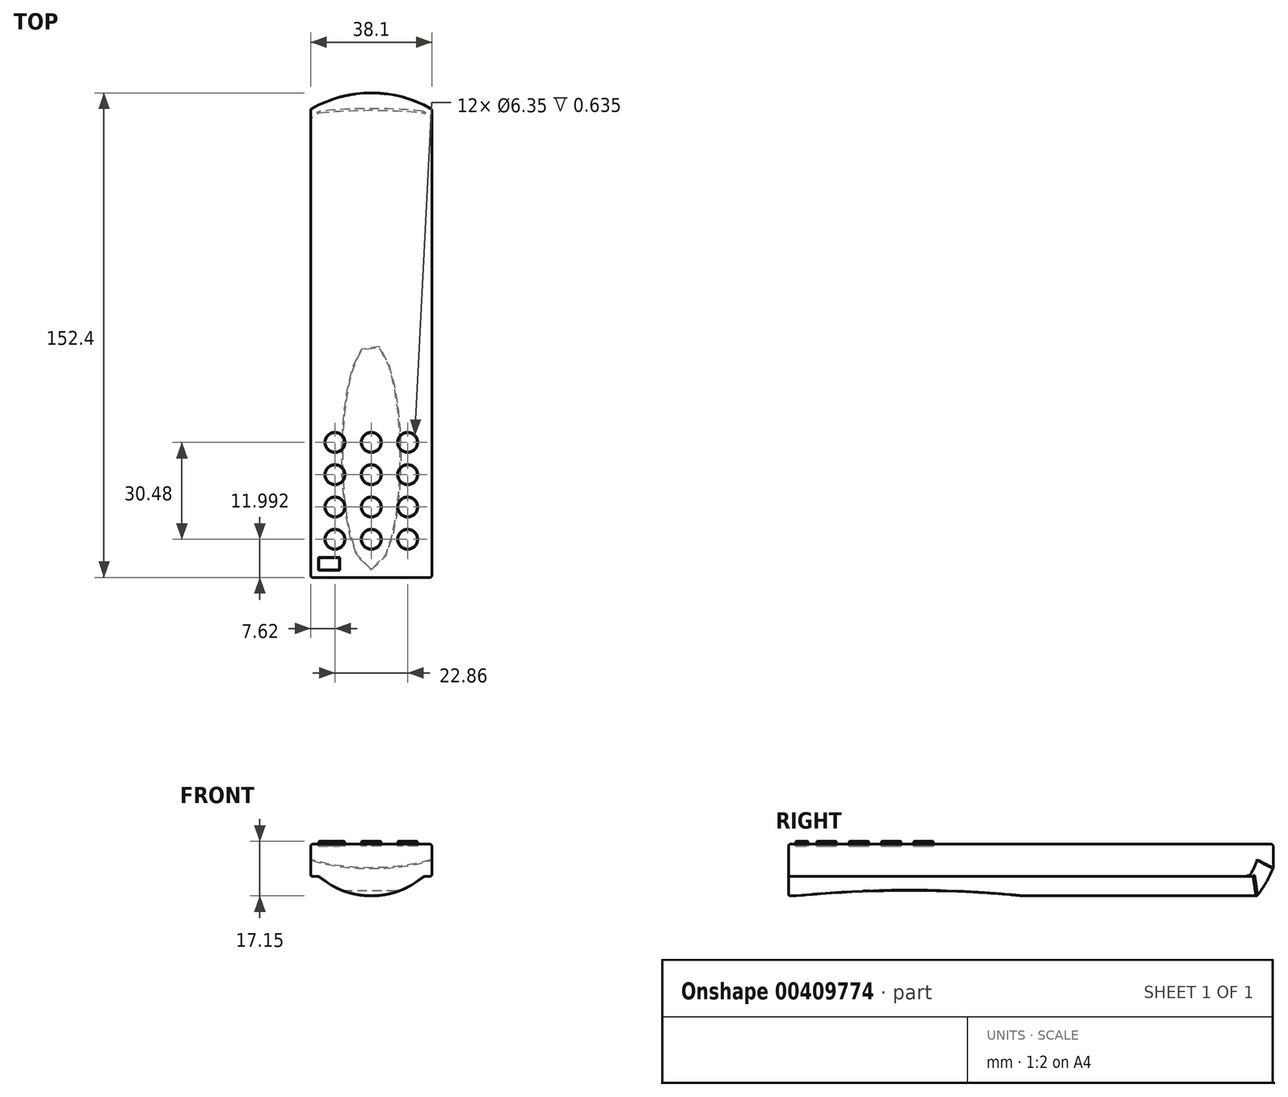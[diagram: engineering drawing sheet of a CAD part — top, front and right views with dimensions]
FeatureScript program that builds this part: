
annotation { "Feature Type Name" : "Feature", "Feature Type Description" : "" }
export const myFeature = defineFeature(function(context is Context, id is Id, definition is map)
    precondition{}
    {
        {
            var Q0;
            Q0=qCreatedBy(makeId("Front.planeOp"),FACE);
            var sketch = newSketch(context, id + "F0", { "sketchPlane" : qUnion([Q0])});
            skLineSegment(sketch, "E0.bottom", {"start": v(19.05, 5.08) * mm, "end": v(-19.05, 5.08) * mm});
            skLineSegment(sketch, "E0.top", {"start": v(19.05, -5.08) * mm, "end": v(-19.05, -5.08) * mm});
            skLineSegment(sketch, "E0.left", {"start": v(19.05, 5.08) * mm, "end": v(19.05, -5.08) * mm});
            skLineSegment(sketch, "E0.right", {"start": v(-19.05, 5.08) * mm, "end": v(-19.05, -5.08) * mm});
            skPoint(sketch, "E0.middle", {"position": v(0, 0) * mm});
            skArc(sketch, "E1", {"start": v(-16.51, -5.08) * mm, "mid": v(0, -11.18) * mm, "end": v(16.5, -5.08) * mm});
            skSolve(sketch);
        }
        {
            var Q0;
            Q0 = qSketchRegion(id + "F0", true);
            extrude(context, id + "F1", {"entities" : qUnion([Q0]), "depth" : 152.4 * mm, "symmetric" : true});
        }
        {
            var Q0;
            Q0=makeQuery(id+"F1.opExtrude","SWEPT_FACE",FACE,{"disambiguationData":[OSD([sQuery(id+"F0.wireOp",EDGE,"E0.bottom")])]});
            var sketch = newSketch(context, id + "F2", { "sketchPlane" : qUnion([Q0])});
            skArc(sketch, "E2", {"start": v(19.05, 71.1) * mm, "mid": v(0, 76.2) * mm, "end": v(-19.05, 71.1) * mm});
            skLineSegment(sketch, "E3", {"start": v(0, -0.47) * mm, "end": v(0, 76.2) * mm, "construction": true});
            skSolve(sketch);
        }
        {
            var Q0;
            {var subQ0=sQuery(id+"F2.wireOp",EDGE,"E2");var subQ1=sQuery(id+"F0.wireOp",EDGE,"E0.bottom");var subQ4=makeQuery(id+"F1.opExtrude","CAP_EDGE",EDGE,{"disambiguationData":[OSD([subQ1])],"isStart":true});var subQ5=makeQuery(id+"F2.imprint","INTERSECT",VERTEX,{"derivedFrom":[subQ4,subQ0]});Q0=makeQuery(id+"F2.imprint","IMPRINT",FACE,{"disambiguationData":[TD([[makeQuery(id+"F2.imprint","IMPRINT",EDGE,{"disambiguationData":[TD([[subQ5,1.0]])],"derivedFrom":subQ0}),-1.0]])]});}
            var Q1;
            {var subQ0=sQuery(id+"F2.wireOp",EDGE,"E2");var subQ1=sQuery(id+"F0.wireOp",EDGE,"E0.bottom");var subQ4=makeQuery(id+"F1.opExtrude","CAP_EDGE",EDGE,{"disambiguationData":[OSD([subQ1])],"isStart":true});var subQ5=makeQuery(id+"F2.imprint","INTERSECT",VERTEX,{"derivedFrom":[subQ4,subQ0]});Q1=makeQuery(id+"F2.imprint","IMPRINT",FACE,{"disambiguationData":[TD([[makeQuery(id+"F2.imprint","IMPRINT",EDGE,{"disambiguationData":[TD([[subQ5,-1.0]])],"derivedFrom":subQ0}),-1.0]])]});}
            extrude(context, id + "F3", {"entities" : qUnion([Q0, Q1]), "operationType" : NewBodyOperationType.REMOVE, "endBound" : BoundingType.THROUGH_ALL, "oppositeDirection" : true, "depth" : 25.4 * mm});
        }
        {
            var Q0;
            Q0=qCreatedBy(makeId("Right.planeOp"),FACE);
            var sketch = newSketch(context, id + "F4", { "sketchPlane" : qUnion([Q0])});
            skArc(sketch, "E4", {"start": v(64.41, -17.52) * mm, "mid": v(76.76, -0.97) * mm, "end": v(77.47, 19.67) * mm});
            skCircle(sketch, "E5", {"center": v(44.14, 10.48) * mm, "radius": 34.57 * mm});
            skLineSegment(sketch, "E6", {"start": v(44.14, 45.05) * mm, "end": v(44.14, -24.1) * mm});
            skLineSegment(sketch, "E7.bottom", {"start": v(44.14, 45.05) * mm, "end": v(78.38, 45.05) * mm});
            skLineSegment(sketch, "E7.top", {"start": v(44.14, -24.1) * mm, "end": v(78.38, -24.1) * mm});
            skLineSegment(sketch, "E7.right", {"start": v(78.38, 45.05) * mm, "end": v(78.38, -24.1) * mm});
            skSolve(sketch);
        }
        {
            var Q0;
            {var subQ0=sQuery(id+"F4.wireOp",EDGE,"E7.top");Q0=makeQuery(id+"F4.imprint","IMPRINT",FACE,{"disambiguationData":[TD([[makeQuery(id+"F4.imprint","IMPRINT",EDGE,{"derivedFrom":subQ0}),1.0]])]});}
            var Q1;
            Q1=sQuery(id+"F4.wireOp",EDGE,"E6");
            revolve(context, id + "F5", {"operationType" : NewBodyOperationType.REMOVE, "entities" : qUnion([Q0]), "axis" : qUnion([Q1]), "revolveType" : RevolveType.SYMMETRIC, "oppositeDirection" : true, "angle" : 90 * degree});
        }
        {
            var Q0;
            Q0=makeQuery(id+"F5.boolean.opBoolean","COPY",FACE,{"derivedFrom":makeQuery(id+"F5.opRevolve","SWEPT_FACE",FACE,{"disambiguationData":[OSD([sQuery(id+"F4.wireOp",EDGE,"E5")])]})});
            var Q1;
            {var subQ0=sQuery(id+"F2.wireOp",EDGE,"E2");var subQ1=sQuery(id+"F0.wireOp",EDGE,"E0.bottom");var subQ2=makeQuery(id+"F2.imprint","INTERSECT",VERTEX,{"derivedFrom":[makeQuery(id+"F1.opExtrude","CAP_EDGE",EDGE,{"disambiguationData":[OSD([subQ1])],"isStart":true}),subQ0]});Q1=makeQuery(id+"F3.boolean.opBoolean","MERGE",FACE,{"derivedFrom":[],"fromTools":[makeQuery(id+"F3.opExtrude","SWEPT_FACE",FACE,{"disambiguationData":[OSD([subQ0]),TDD([makeQuery(id+"F2.imprint","IMPRINT",EDGE,{"disambiguationData":[TD([[subQ2,1.0]])],"derivedFrom":subQ0})])]}),makeQuery(id+"F3.opExtrude","SWEPT_FACE",FACE,{"disambiguationData":[OSD([subQ0]),TDD([makeQuery(id+"F2.imprint","IMPRINT",EDGE,{"disambiguationData":[TD([[subQ2,-1.0]])],"derivedFrom":subQ0})])]})]});}
            var Q2;
            Q2=makeQuery(id+"F1.opExtrude","SWEPT_FACE",FACE,{"disambiguationData":[OSD([sQuery(id+"F0.wireOp",EDGE,"E0.bottom")])]});
            var Q3;
            Q3=makeQuery(id+"F1.opExtrude","SWEPT_FACE",FACE,{"disambiguationData":[OSD([sQuery(id+"F0.wireOp",EDGE,"E0.right")])]});
            var Q4;
            Q4=makeQuery(id+"F1.opExtrude","SWEPT_FACE",FACE,{"disambiguationData":[OSD([sQuery(id+"F0.wireOp",EDGE,"E1")])]});
            var Q5;
            {var subQ0=sQuery(id+"F0.wireOp",EDGE,"E0.top");Q5=makeQuery(id+"F1.opExtrude","SWEPT_FACE",FACE,{"disambiguationData":[OSD([subQ0]),TDD([makeQuery(id+"F0.imprint","IMPRINT",EDGE,{"disambiguationData":[TD([[makeQuery(id+"F0.imprint","INTERSECT",VERTEX,{"derivedFrom":[subQ0,sQuery(id+"F0.wireOp",EDGE,"E0.right")]}),1.0]])],"derivedFrom":subQ0})])]});}
            var Q6;
            {var subQ0=sQuery(id+"F0.wireOp",EDGE,"E0.top");Q6=makeQuery(id+"F1.opExtrude","SWEPT_FACE",FACE,{"disambiguationData":[OSD([subQ0]),TDD([makeQuery(id+"F0.imprint","IMPRINT",EDGE,{"disambiguationData":[TD([[makeQuery(id+"F0.imprint","INTERSECT",VERTEX,{"derivedFrom":[subQ0,sQuery(id+"F0.wireOp",EDGE,"E0.left")]}),-1.0]])],"derivedFrom":subQ0})])]});}
            var Q7;
            Q7=makeQuery(id+"F1.opExtrude","SWEPT_FACE",FACE,{"disambiguationData":[OSD([sQuery(id+"F0.wireOp",EDGE,"E0.left")])]});
            var Q8;
            Q8=makeQuery(id+"F1.opExtrude","CAP_FACE",FACE,{"disambiguationData":[OSD([sQuery(id+"F0.wireOp",EDGE,"E0.bottom"),sQuery(id+"F0.wireOp",EDGE,"E0.top"),sQuery(id+"F0.wireOp",EDGE,"E0.left"),sQuery(id+"F0.wireOp",EDGE,"E0.right"),sQuery(id+"F0.wireOp",EDGE,"E1")])],"isStart":false});
            fillet(context, id + "F6", {"entities" : qUnion([Q0, Q1, Q2, Q3, Q4, Q5, Q6, Q7, Q8]), "radius" : 0.64 * mm, "tangentPropagation" : true, "allowEdgeOverflow" : false});
        }
        {
            var Q0;
            Q0=makeQuery(id+"F1.opExtrude","SWEPT_FACE",FACE,{"disambiguationData":[OSD([sQuery(id+"F0.wireOp",EDGE,"E0.bottom")])]});
            var sketch = newSketch(context, id + "F7", { "sketchPlane" : qUnion([Q0])});
            skLineSegment(sketch, "E8.bottom", {"start": v(-16.6, -74) * mm, "end": v(-9.92, -74) * mm});
            skLineSegment(sketch, "E8.top", {"start": v(-16.6, -69.92) * mm, "end": v(-9.92, -69.92) * mm});
            skLineSegment(sketch, "E8.left", {"start": v(-16.6, -74) * mm, "end": v(-16.6, -69.92) * mm});
            skLineSegment(sketch, "E8.right", {"start": v(-9.92, -74) * mm, "end": v(-9.92, -69.92) * mm});
            skCircle(sketch, "E9", {"center": v(11.43, -64.2) * mm, "radius": 3.18 * mm});
            skCircle(sketch, "E10.0.1.0", {"center": v(11.43, -54.05) * mm, "radius": 3.18 * mm});
            skCircle(sketch, "E10.0.2.0", {"center": v(11.43, -43.89) * mm, "radius": 3.18 * mm});
            skCircle(sketch, "E10.0.3.0", {"center": v(11.43, -33.73) * mm, "radius": 3.18 * mm});
            skCircle(sketch, "E10.1.0.0", {"center": v(0, -64.2) * mm, "radius": 3.18 * mm});
            skCircle(sketch, "E10.1.1.0", {"center": v(0, -54.05) * mm, "radius": 3.18 * mm});
            skCircle(sketch, "E10.1.2.0", {"center": v(0, -43.89) * mm, "radius": 3.18 * mm});
            skCircle(sketch, "E10.1.3.0", {"center": v(0, -33.73) * mm, "radius": 3.18 * mm});
            skCircle(sketch, "E10.2.0.0", {"center": v(-11.43, -64.2) * mm, "radius": 3.18 * mm});
            skCircle(sketch, "E10.2.1.0", {"center": v(-11.43, -54.05) * mm, "radius": 3.18 * mm});
            skCircle(sketch, "E10.2.2.0", {"center": v(-11.43, -43.89) * mm, "radius": 3.18 * mm});
            skCircle(sketch, "E10.2.3.0", {"center": v(-11.43, -33.73) * mm, "radius": 3.18 * mm});
            skLineSegment(sketch, "E10.direction1", {"start": v(11.43, -64.2) * mm, "end": v(0, -64.2) * mm, "construction": true});
            skLineSegment(sketch, "E10.direction2", {"start": v(11.43, -64.2) * mm, "end": v(11.43, -54.05) * mm, "construction": true});
            skSolve(sketch);
        }
        {
            var Q0;
            Q0 = qSketchRegion(id + "F7", true);
            extrude(context, id + "F8", {"entities" : qUnion([Q0]), "operationType" : NewBodyOperationType.REMOVE, "oppositeDirection" : true, "depth" : 0.64 * mm});
        }
        {
            var Q0;
            Q0=makeQuery(id+"F8.boolean.opBoolean","COPY",FACE,{"derivedFrom":makeQuery(id+"F8.opExtrude","CAP_FACE",FACE,{"disambiguationData":[OSD([sQuery(id+"F7.wireOp",EDGE,"E8.bottom"),sQuery(id+"F7.wireOp",EDGE,"E8.top"),sQuery(id+"F7.wireOp",EDGE,"E8.left"),sQuery(id+"F7.wireOp",EDGE,"E8.right")])],"isStart":false})});
            var sketch = newSketch(context, id + "F9", { "sketchPlane" : qUnion([Q0])});
            skLineSegment(sketch, "E11.bottom", {"start": v(-9.92, -74) * mm, "end": v(-16.6, -74) * mm});
            skLineSegment(sketch, "E11.top", {"start": v(-9.92, -69.92) * mm, "end": v(-16.6, -69.92) * mm});
            skLineSegment(sketch, "E11.left", {"start": v(-9.92, -74) * mm, "end": v(-9.92, -69.92) * mm});
            skLineSegment(sketch, "E11.right", {"start": v(-16.6, -74) * mm, "end": v(-16.6, -69.92) * mm});
            skLineSegment(sketch, "E12.bottom", {"start": v(-10.05, -73.87) * mm, "end": v(-16.48, -73.87) * mm});
            skLineSegment(sketch, "E12.top", {"start": v(-10.05, -70.05) * mm, "end": v(-16.48, -70.05) * mm});
            skLineSegment(sketch, "E12.left", {"start": v(-10.05, -73.87) * mm, "end": v(-10.05, -70.05) * mm});
            skLineSegment(sketch, "E12.right", {"start": v(-16.48, -73.87) * mm, "end": v(-16.48, -70.05) * mm});
            skPoint(sketch, "E12.middle", {"position": v(-13.26, -71.96) * mm});
            skPoint(sketch, "E12.middle.positionSnap0", {"position": v(-16.6, -71.96) * mm});
            skPoint(sketch, "E12.middle.positionSnap1", {"position": v(-13.26, -74) * mm});
            skPoint(sketch, "E12.centerSnap0", {"position": v(-16.6, -71.96) * mm});
            skPoint(sketch, "E12.centerSnap1", {"position": v(-13.26, -74) * mm});
            skCircle(sketch, "E13", {"center": v(11.43, -64.2) * mm, "radius": 3.05 * mm});
            skCircle(sketch, "E14.0.1.0", {"center": v(11.43, -54.05) * mm, "radius": 3.05 * mm});
            skCircle(sketch, "E14.0.2.0", {"center": v(11.43, -43.89) * mm, "radius": 3.05 * mm});
            skCircle(sketch, "E14.0.3.0", {"center": v(11.43, -33.73) * mm, "radius": 3.05 * mm});
            skCircle(sketch, "E14.1.0.0", {"center": v(0, -64.2) * mm, "radius": 3.05 * mm});
            skCircle(sketch, "E14.1.1.0", {"center": v(0, -54.05) * mm, "radius": 3.05 * mm});
            skCircle(sketch, "E14.1.2.0", {"center": v(0, -43.89) * mm, "radius": 3.05 * mm});
            skCircle(sketch, "E14.1.3.0", {"center": v(0, -33.73) * mm, "radius": 3.05 * mm});
            skCircle(sketch, "E14.2.0.0", {"center": v(-11.43, -64.2) * mm, "radius": 3.05 * mm});
            skCircle(sketch, "E14.2.1.0", {"center": v(-11.43, -54.05) * mm, "radius": 3.05 * mm});
            skCircle(sketch, "E14.2.2.0", {"center": v(-11.43, -43.89) * mm, "radius": 3.05 * mm});
            skCircle(sketch, "E14.2.3.0", {"center": v(-11.43, -33.73) * mm, "radius": 3.05 * mm});
            skLineSegment(sketch, "E14.direction1", {"start": v(11.43, -64.2) * mm, "end": v(0, -64.2) * mm, "construction": true});
            skLineSegment(sketch, "E14.direction2", {"start": v(11.43, -64.2) * mm, "end": v(11.43, -54.05) * mm, "construction": true});
            skSolve(sketch);
        }
        {
            var Q0;
            Q0=makeQuery(id+"F9.imprint","IMPRINT",FACE,{"disambiguationData":[TD([[makeQuery(id+"F9.imprint","IMPRINT",EDGE,{"derivedFrom":sQuery(id+"F9.wireOp",EDGE,"E12.bottom")}),-1.0]])]});
            var Q1;
            Q1=makeQuery(id+"F9.imprint","IMPRINT",FACE,{"disambiguationData":[TD([[makeQuery(id+"F9.imprint","IMPRINT",EDGE,{"derivedFrom":sQuery(id+"F9.wireOp",EDGE,"E14.2.0.0")}),1.0]])]});
            var Q2;
            Q2=makeQuery(id+"F9.imprint","IMPRINT",FACE,{"disambiguationData":[TD([[makeQuery(id+"F9.imprint","IMPRINT",EDGE,{"derivedFrom":sQuery(id+"F9.wireOp",EDGE,"E14.1.0.0")}),1.0]])]});
            var Q3;
            Q3=makeQuery(id+"F9.imprint","IMPRINT",FACE,{"disambiguationData":[TD([[makeQuery(id+"F9.imprint","IMPRINT",EDGE,{"derivedFrom":sQuery(id+"F9.wireOp",EDGE,"E13")}),1.0]])]});
            var Q4;
            Q4=makeQuery(id+"F9.imprint","IMPRINT",FACE,{"disambiguationData":[TD([[makeQuery(id+"F9.imprint","IMPRINT",EDGE,{"derivedFrom":sQuery(id+"F9.wireOp",EDGE,"E14.0.1.0")}),1.0]])]});
            var Q5;
            Q5=makeQuery(id+"F9.imprint","IMPRINT",FACE,{"disambiguationData":[TD([[makeQuery(id+"F9.imprint","IMPRINT",EDGE,{"derivedFrom":sQuery(id+"F9.wireOp",EDGE,"E14.1.1.0")}),1.0]])]});
            var Q6;
            Q6=makeQuery(id+"F9.imprint","IMPRINT",FACE,{"disambiguationData":[TD([[makeQuery(id+"F9.imprint","IMPRINT",EDGE,{"derivedFrom":sQuery(id+"F9.wireOp",EDGE,"E14.2.1.0")}),1.0]])]});
            var Q7;
            Q7=makeQuery(id+"F9.imprint","IMPRINT",FACE,{"disambiguationData":[TD([[makeQuery(id+"F9.imprint","IMPRINT",EDGE,{"derivedFrom":sQuery(id+"F9.wireOp",EDGE,"E14.2.2.0")}),1.0]])]});
            var Q8;
            Q8=makeQuery(id+"F9.imprint","IMPRINT",FACE,{"disambiguationData":[TD([[makeQuery(id+"F9.imprint","IMPRINT",EDGE,{"derivedFrom":sQuery(id+"F9.wireOp",EDGE,"E14.1.2.0")}),1.0]])]});
            var Q9;
            Q9=makeQuery(id+"F9.imprint","IMPRINT",FACE,{"disambiguationData":[TD([[makeQuery(id+"F9.imprint","IMPRINT",EDGE,{"derivedFrom":sQuery(id+"F9.wireOp",EDGE,"E14.0.2.0")}),1.0]])]});
            var Q10;
            Q10=makeQuery(id+"F9.imprint","IMPRINT",FACE,{"disambiguationData":[TD([[makeQuery(id+"F9.imprint","IMPRINT",EDGE,{"derivedFrom":sQuery(id+"F9.wireOp",EDGE,"E14.0.3.0")}),1.0]])]});
            var Q11;
            Q11=makeQuery(id+"F9.imprint","IMPRINT",FACE,{"disambiguationData":[TD([[makeQuery(id+"F9.imprint","IMPRINT",EDGE,{"derivedFrom":sQuery(id+"F9.wireOp",EDGE,"E14.1.3.0")}),1.0]])]});
            var Q12;
            Q12=makeQuery(id+"F9.imprint","IMPRINT",FACE,{"disambiguationData":[TD([[makeQuery(id+"F9.imprint","IMPRINT",EDGE,{"derivedFrom":sQuery(id+"F9.wireOp",EDGE,"E14.2.3.0")}),1.0]])]});
            extrude(context, id + "F10", {"entities" : qUnion([Q0, Q1, Q2, Q3, Q4, Q5, Q6, Q7, Q8, Q9, Q10, Q11, Q12]), "operationType" : NewBodyOperationType.ADD, "depth" : 1.52 * mm});
        }
        {
            var Q0;
            Q0=makeQuery(id+"F10.opExtrude","SWEPT_EDGE",EDGE,{"disambiguationData":[OSD([sQuery(id+"F9.wireOp",EDGE,"E12.bottom"),sQuery(id+"F9.wireOp",EDGE,"E12.right")])]});
            var Q1;
            Q1=makeQuery(id+"F10.opExtrude","SWEPT_EDGE",EDGE,{"disambiguationData":[OSD([sQuery(id+"F9.wireOp",EDGE,"E12.top"),sQuery(id+"F9.wireOp",EDGE,"E12.right")])]});
            var Q2;
            Q2=makeQuery(id+"F10.opExtrude","SWEPT_EDGE",EDGE,{"disambiguationData":[OSD([sQuery(id+"F9.wireOp",EDGE,"E12.top"),sQuery(id+"F9.wireOp",EDGE,"E12.left")])]});
            var Q3;
            Q3=makeQuery(id+"F10.opExtrude","SWEPT_EDGE",EDGE,{"disambiguationData":[OSD([sQuery(id+"F9.wireOp",EDGE,"E12.bottom"),sQuery(id+"F9.wireOp",EDGE,"E12.left")])]});
            fillet(context, id + "F11", {"entities" : qUnion([Q0, Q1, Q2, Q3]), "radius" : 0.25 * mm, "tangentPropagation" : true, "allowEdgeOverflow" : false});
        }
        {
            var Q0;
            Q0=makeQuery(id+"F10.opExtrude","CAP_FACE",FACE,{"disambiguationData":[OSD([sQuery(id+"F9.wireOp",EDGE,"E12.bottom"),sQuery(id+"F9.wireOp",EDGE,"E12.top"),sQuery(id+"F9.wireOp",EDGE,"E12.left"),sQuery(id+"F9.wireOp",EDGE,"E12.right")])],"isStart":false});
            var Q1;
            Q1=makeQuery(id+"F10.opExtrude","CAP_FACE",FACE,{"disambiguationData":[OSD([sQuery(id+"F9.wireOp",EDGE,"E14.2.0.0")])],"isStart":false});
            var Q2;
            Q2=makeQuery(id+"F10.opExtrude","CAP_FACE",FACE,{"disambiguationData":[OSD([sQuery(id+"F9.wireOp",EDGE,"E14.1.0.0")])],"isStart":false});
            var Q3;
            Q3=makeQuery(id+"F10.opExtrude","CAP_FACE",FACE,{"disambiguationData":[OSD([sQuery(id+"F9.wireOp",EDGE,"E13")])],"isStart":false});
            var Q4;
            Q4=makeQuery(id+"F10.opExtrude","CAP_FACE",FACE,{"disambiguationData":[OSD([sQuery(id+"F9.wireOp",EDGE,"E14.0.1.0")])],"isStart":false});
            var Q5;
            Q5=makeQuery(id+"F10.opExtrude","CAP_FACE",FACE,{"disambiguationData":[OSD([sQuery(id+"F9.wireOp",EDGE,"E14.1.1.0")])],"isStart":false});
            var Q6;
            Q6=makeQuery(id+"F10.opExtrude","CAP_FACE",FACE,{"disambiguationData":[OSD([sQuery(id+"F9.wireOp",EDGE,"E14.2.1.0")])],"isStart":false});
            var Q7;
            Q7=makeQuery(id+"F10.opExtrude","CAP_FACE",FACE,{"disambiguationData":[OSD([sQuery(id+"F9.wireOp",EDGE,"E14.2.2.0")])],"isStart":false});
            var Q8;
            Q8=makeQuery(id+"F10.opExtrude","CAP_FACE",FACE,{"disambiguationData":[OSD([sQuery(id+"F9.wireOp",EDGE,"E14.2.3.0")])],"isStart":false});
            var Q9;
            Q9=makeQuery(id+"F10.opExtrude","CAP_FACE",FACE,{"disambiguationData":[OSD([sQuery(id+"F9.wireOp",EDGE,"E14.1.3.0")])],"isStart":false});
            var Q10;
            Q10=makeQuery(id+"F10.opExtrude","CAP_FACE",FACE,{"disambiguationData":[OSD([sQuery(id+"F9.wireOp",EDGE,"E14.1.2.0")])],"isStart":false});
            var Q11;
            Q11=makeQuery(id+"F10.opExtrude","CAP_FACE",FACE,{"disambiguationData":[OSD([sQuery(id+"F9.wireOp",EDGE,"E14.0.2.0")])],"isStart":false});
            var Q12;
            Q12=makeQuery(id+"F10.opExtrude","CAP_FACE",FACE,{"disambiguationData":[OSD([sQuery(id+"F9.wireOp",EDGE,"E14.0.3.0")])],"isStart":false});
            fillet(context, id + "F12", {"entities" : qUnion([Q0, Q1, Q2, Q3, Q4, Q5, Q6, Q7, Q8, Q9, Q10, Q11, Q12]), "radius" : 0.13 * mm, "tangentPropagation" : true, "allowEdgeOverflow" : false});
        }
        {
            var Q0;
            Q0=qCreatedBy(makeId("Right.planeOp"),FACE);
            var sketch = newSketch(context, id + "F13", { "sketchPlane" : qUnion([Q0])});
            skCircle(sketch, "E15", {"center": v(-38.1, -381) * mm, "radius": 371.54 * mm});
            skSolve(sketch);
        }
        {
            var Q0;
            Q0=makeQuery(id+"F13.imprint","IMPRINT",FACE,{"disambiguationData":[TD([[makeQuery(id+"F13.imprint","IMPRINT",EDGE,{"derivedFrom":sQuery(id+"F13.wireOp",EDGE,"E15")}),1.0]])]});
            extrude(context, id + "F14", {"entities" : qUnion([Q0]), "operationType" : NewBodyOperationType.REMOVE, "oppositeDirection" : true, "depth" : 50.8 * mm, "symmetric" : true});
        }
        {
            var Q0;
            Q0=makeQuery(id+"F14.boolean.opBoolean","INTERSECT",EDGE,{"derivedFrom":[makeQuery(id+"F1.opExtrude","SWEPT_FACE",FACE,{"disambiguationData":[OSD([sQuery(id+"F0.wireOp",EDGE,"E1")])]}),makeQuery(id+"F14.opExtrude","SWEPT_FACE",FACE,{"disambiguationData":[OSD([sQuery(id+"F13.wireOp",EDGE,"E15")])]})]});
            fillet(context, id + "F15", {"entities" : qUnion([Q0]), "radius" : 1.27 * mm, "tangentPropagation" : true, "allowEdgeOverflow" : false});
        }
    });
